# Revit family: BC_URMET_MONITEUR-HBS-V2_LOD2000
name_source: partatom
category: Appareils de communication
revit_build: Autodesk Revit 2017 (Build: 20181011_1645(x64)
units: mm (PartAtom-declared; Revit-internal decimal feet)

## family parameters
Conserver l'orientation des annotations = Non
Cote de connecteur circulaire = Utiliser le diamètre
Couper avec des vides une fois chargée = Non
Hôte = Face
Numéro OmniClass = 23.85.50.14.21
Partagée = Non
Point de calcul de pièce = Non
Titre OmniClass = Intercommunication Equipment
Type d'élément = Normal

## types (1)
- URMET - MONITEUR HBS V2
    Boucle magnétique intégrée = Oui
    Code Produit = MHBSV2
    Commentaires du type = MONITEUR HBS V2
    Description = Moniteur main libre vidéo tactile 7 pouces
    Ecran tactile = Oui
    Elévation par défaut = 1219.2 mm  [stored 4 ft]
    Epaisseur Hors Tout = 36 mm  [stored 0.11811 ft]
    Fabricant = URMET
    Haut-parleur = Oui
    Largeur Hors Tout = 169 mm  [stored 0.554462 ft]
    Lecteur de badge = Oui
    Longueur Hors Tout = 210 mm  [stored 0.688976 ft]
    Masse = 0.66 kg
    Microphone = Oui
    Mise en veille et allumage = Oui
    Modèle = MONITEUR HBS V2
    Ouverture porte = Oui
    Réglage du volume = Oui
    Taille de l'écran = 7"
    URL = www.urmet.fr
    Voyant alerte = Oui
    Voyant coupure de sonnerie = Oui
    Voyant message = Oui
    Voyant scenario Actif = Oui

note: [stored X ft] marks values corroborated as IEEE doubles in the binary element streams (Revit-internal decimal feet)
